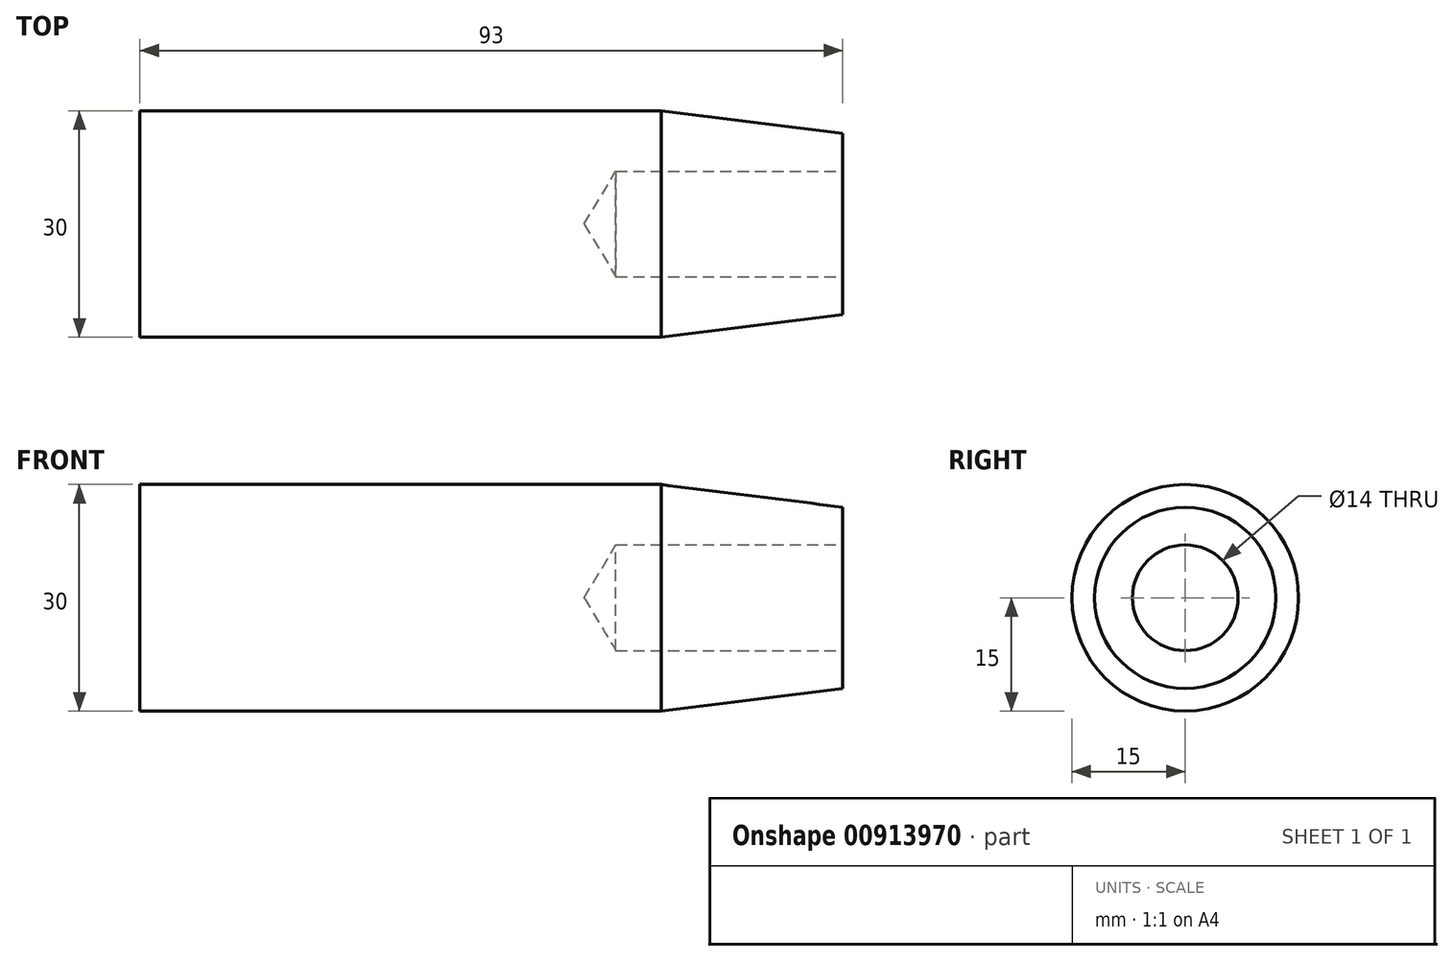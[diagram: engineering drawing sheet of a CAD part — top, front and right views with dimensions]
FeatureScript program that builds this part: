
annotation { "Feature Type Name" : "Feature", "Feature Type Description" : "" }
export const myFeature = defineFeature(function(context is Context, id is Id, definition is map)
    precondition{}
    {
        {
            var Q0;
            Q0=qCreatedBy(makeId("Front.planeOp"),FACE);
            var sketch = newSketch(context, id + "F0", { "sketchPlane" : qUnion([Q0])});
            skLineSegment(sketch, "E0", {"start": v(-60.49, 0) * mm, "end": v(70.04, 0) * mm});
            skLineSegment(sketch, "E1.bottom", {"start": v(-54.2, 0) * mm, "end": v(-42.2, 0) * mm});
            skLineSegment(sketch, "E1.top", {"start": v(-54.2, 21) * mm, "end": v(-42.2, 21) * mm});
            skLineSegment(sketch, "E1.left", {"start": v(-54.2, 0) * mm, "end": v(-54.2, 21) * mm});
            skLineSegment(sketch, "E1.right", {"start": v(-42.2, 0) * mm, "end": v(-42.2, 21) * mm});
            skLineSegment(sketch, "E2.bottom", {"start": v(-42.2, 0) * mm, "end": v(26.8, 0) * mm});
            skLineSegment(sketch, "E2.top", {"start": v(-42.2, 15) * mm, "end": v(26.8, 15) * mm});
            skLineSegment(sketch, "E2.left", {"start": v(-42.2, 0) * mm, "end": v(-42.2, 15) * mm});
            skLineSegment(sketch, "E2.right", {"start": v(26.8, 0) * mm, "end": v(26.8, 15) * mm});
            skLineSegment(sketch, "E3", {"start": v(50.8, 0) * mm, "end": v(50.8, 12) * mm});
            skLineSegment(sketch, "E4", {"start": v(50.8, 12) * mm, "end": v(26.8, 15) * mm});
            skPoint(sketch, "E5.end.orphan", {"position": v(20.8, 0) * mm});
            skPoint(sketch, "E6.orphan", {"position": v(-24.2, 9) * mm});
            skPoint(sketch, "E7.0.end.orphan", {"position": v(-24.2, 18) * mm});
            skLineSegment(sketch, "E8", {"start": v(-54.2, 0) * mm, "end": v(-20.79, 0) * mm});
            skSolve(sketch);
        }
        {
            var Q0;
            Q0=makeQuery(id+"F0.imprint","IMPRINT",FACE,{"disambiguationData":[TD([[makeQuery(id+"F0.imprint","IMPRINT",EDGE,{"derivedFrom":sQuery(id+"F0.wireOp",EDGE,"E1.bottom")}),1.0]])]});
            var Q1;
            {var subQ0=sQuery(id+"F0.wireOp",EDGE,"E2.top");Q1=makeQuery(id+"F0.imprint","IMPRINT",FACE,{"disambiguationData":[TD([[makeQuery(id+"F0.imprint","IMPRINT",EDGE,{"derivedFrom":subQ0}),-1.0]])]});}
            var Q2;
            {var subQ0=sQuery(id+"F0.wireOp",EDGE,"E2.right");Q2=makeQuery(id+"F0.imprint","IMPRINT",FACE,{"disambiguationData":[TD([[makeQuery(id+"F0.imprint","IMPRINT",EDGE,{"derivedFrom":subQ0}),-1.0]])]});}
            var Q3;
            Q3=sQuery(id+"F0.wireOp",EDGE,"E0");
            revolve(context, id + "F1", {"surfaceOperationType" : NewSurfaceOperationType.NEW, "entities" : qUnion([Q0, Q1, Q2]), "axis" : qUnion([Q3]), "revolveType" : RevolveType.FULL});
        }
        {
            var Q0;
            Q0=makeQuery(id+"F1.opRevolve","SWEPT_FACE",FACE,{"disambiguationData":[OSD([sQuery(id+"F0.wireOp",EDGE,"E3")])]});
            var sketch = newSketch(context, id + "F2", { "sketchPlane" : qUnion([Q0])});
            skCircle(sketch, "E9", {"center": v(0, 0) * mm, "radius": 7 * mm});
            skSolve(sketch);
        }
        {
            var Q0;
            Q0=makeQuery(id+"F2.imprint","IMPRINT",FACE,{"disambiguationData":[TD([[makeQuery(id+"F2.imprint","IMPRINT",EDGE,{"derivedFrom":sQuery(id+"F2.wireOp",EDGE,"E9")}),1.0]])]});
            extrude(context, id + "F3", {"entities" : qUnion([Q0]), "operationType" : NewBodyOperationType.ADD, "oppositeDirection" : true, "depth" : 30 * mm, "offsetDistance" : 25 * mm});
        }
        {
            var Q0;
            Q0=makeQuery(id+"F1.opRevolve","SWEPT_FACE",FACE,{"disambiguationData":[OSD([sQuery(id+"F0.wireOp",EDGE,"E3")])]});
            var sketch = newSketch(context, id + "F4", { "sketchPlane" : qUnion([Q0])});
            skCircle(sketch, "E10", {"center": v(0, 0) * mm, "radius": 7 * mm});
            skSolve(sketch);
        }
        {
            var Q0;
            Q0=sQuery(id+"F4.wireOp",VERTEX,"E10.center");
            var Q1;
            Q1=makeQuery(id+"F1.opRevolve","SWEPT_BODY",BODY,{"disambiguationData":[OSD([sQuery(id+"F0.wireOp",EDGE,"E0"),sQuery(id+"F0.wireOp",EDGE,"E1.right"),sQuery(id+"F0.wireOp",EDGE,"E2.top"),sQuery(id+"F0.wireOp",EDGE,"E3"),sQuery(id+"F0.wireOp",EDGE,"E4")])]});
            hole(context, id + "F5", {"style" : HoleStyle.SIMPLE, "endStyle" : HoleEndStyle.BLIND, "holeDiameter" : 14 * mm, "majorDiameter" : 5 * mm, "holeDepth" : 30 * mm, "isTappedThrough" : true, "tappedDepth" : 12 * mm, "tapClearance" : 3, "locations" : qUnion([Q0]), "scope" : qUnion([Q1])});
        }
    });
